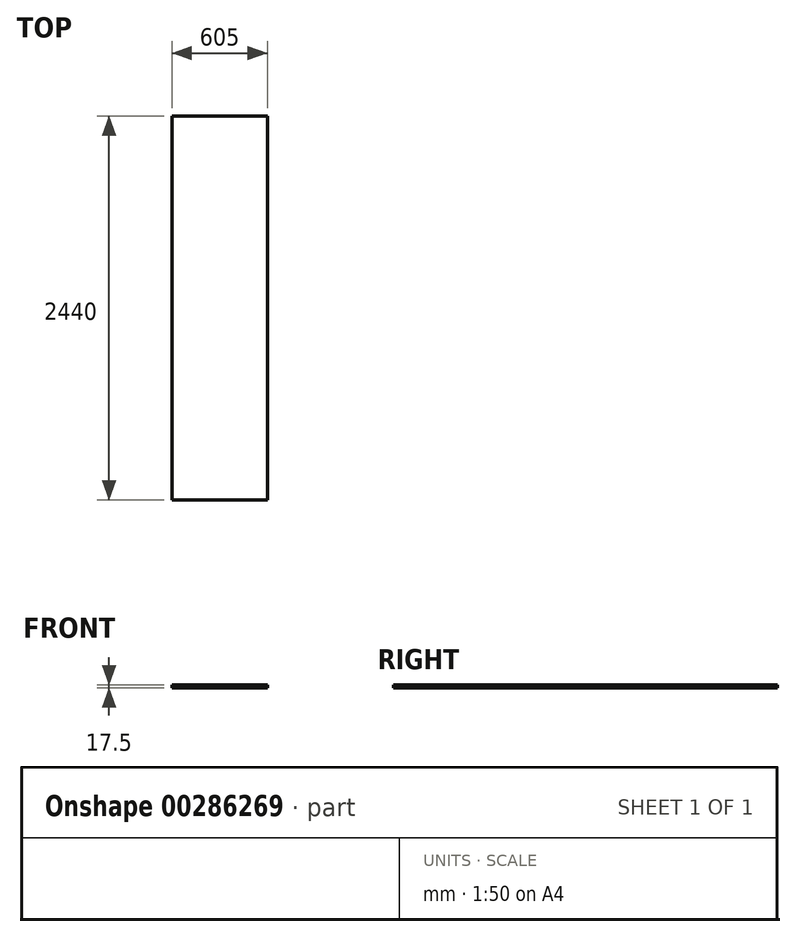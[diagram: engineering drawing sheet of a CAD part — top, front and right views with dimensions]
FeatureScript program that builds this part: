
annotation { "Feature Type Name" : "Feature", "Feature Type Description" : "" }
export const myFeature = defineFeature(function(context is Context, id is Id, definition is map)
    precondition{}
    {
        {
            var Q0;
            Q0=qCreatedBy(makeId("Front.planeOp"),FACE);
            var sketch = newSketch(context, id + "F0", { "sketchPlane" : qUnion([Q0])});
            skLineSegment(sketch, "E0.bottom", {"start": v(-302.5, 9.1) * mm, "end": v(302.5, 9.1) * mm});
            skLineSegment(sketch, "E0.top", {"start": v(-302.5, -8.4) * mm, "end": v(302.5, -8.4) * mm});
            skLineSegment(sketch, "E0.left", {"start": v(-302.5, 9.1) * mm, "end": v(-302.5, -8.4) * mm});
            skLineSegment(sketch, "E0.right", {"start": v(302.5, 9.1) * mm, "end": v(302.5, -8.4) * mm});
            skSolve(sketch);
        }
        {
            var Q0;
            Q0=makeQuery(id+"F0.imprint","IMPRINT",FACE,{"disambiguationData":[TD([[makeQuery(id+"F0.imprint","IMPRINT",EDGE,{"derivedFrom":sQuery(id+"F0.wireOp",EDGE,"E0.bottom")}),-1.0]])]});
            extrude(context, id + "F1", {"entities" : qUnion([Q0]), "depth" : 2440 * mm});
        }
    });
